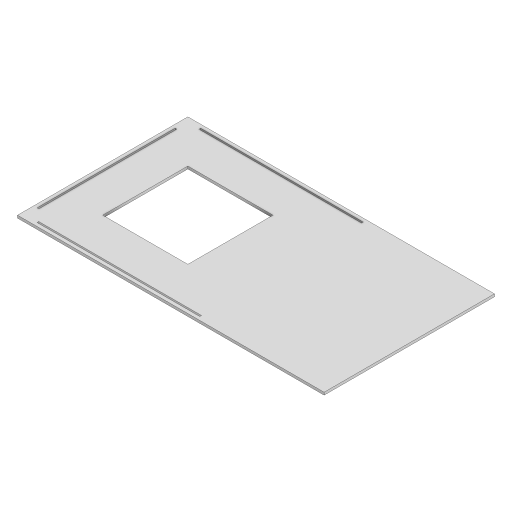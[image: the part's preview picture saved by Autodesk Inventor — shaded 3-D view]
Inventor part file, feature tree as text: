
AUTODESK INVENTOR PART (.ipt)
format: ipt  version: 2024.3 (Build 283343000, 343)  size: 388,608 bytes
history: native  units: mm
features: extrude x2, sketch x2
ambient origin geometry x8: Origin, YZ Plane, XZ Plane, XY Plane, X Axis, Y Axis, Z Axis, Center Point
bodies: Solid1 (feature_tree)
feature tree (4):
  extrude  "Extrusion1"  Depth=100.0mm
  extrude  "Extrusion3"  Depth=50.0mm
  sketch  "Sketch1"  dims[d0=100.0mm d1=100.0mm]
  sketch  "Sketch3"  dims[d2=200.0mm d3=50.0mm d4=210.0mm d5=0.0mm d6=200.0mm d7=3.0mm d8=0.0mm d13=2.0mm d14=2.0mm d15=4.0mm d16=4.0mm d17=4.0mm d18=2.0mm d19=150.0mm d20=2.0mm d21=15.0mm d22=15.0mm d23=15.0mm d24=15.0mm d25=10.0mm d26=0.0mm d27=0.5mm d28=0.872665mm d29=0.5mm d30=0.872665mm]
